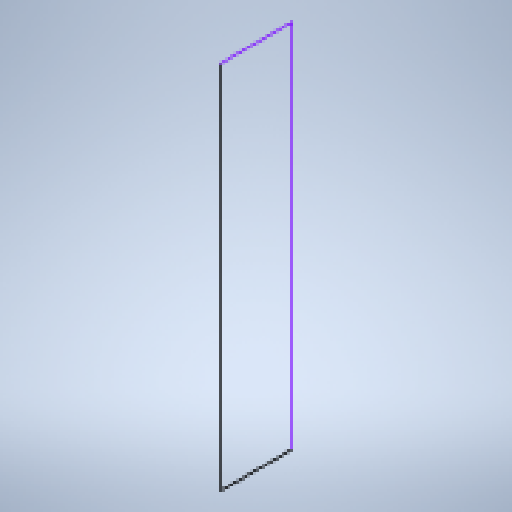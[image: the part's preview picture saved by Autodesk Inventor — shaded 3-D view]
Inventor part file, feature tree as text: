
AUTODESK INVENTOR PART (.ipt)
format: ipt  version: 2023 (Build 270158000, 158)  size: 133,120 bytes
history: native  units: in
note: dims shown in document units (in); Inventor stores cm internally (conversion verified against a paired STEP export)
features: extrude x1, sketch x1
ambient origin geometry x8: Origin, YZ Plane, XZ Plane, XY Plane, X Axis, Y Axis, Z Axis, Center Point
bodies: Solid1 (feature_tree)
feature tree (2):
  extrude  "Extrusion1"  Depth=1.5748in
  sketch  "Sketch1"  dims[d0=9.3622in d1=1.5748in d2=0.1in d3=0.0in]
